# Revit family: EWFLED_AUE03520010001
name_source: partatom
category: Lighting Fixtures
units: mm (PartAtom-declared; Revit-internal decimal feet)

## family parameters
Cut with Voids When Loaded = No
Host = Face
Light Source = Yes
Part Type = Normal
Room Calculation Point = No
Round Connector Dimension = Use Diameter
Shared = No

## types (1)
- EWFLED
    Apparent Load = 240 VA
    Clevertronics Base Angle = 0.00°
    Clevertronics_AS2293 Classification = C0=N/A C90=N/A
    Clevertronics_Annotation Size = 0 mm  [stored 0 ft]
    Clevertronics_Applicable Standards = AS/NZS3820, CISPR15, AS/NZS2293.3
    Clevertronics_Battery = 3.2V 3000mAh
    Clevertronics_Battery Type = Lithium Iron Phosphate
    Clevertronics_Charger Method = Intelligent Current Limited Constant Voltage
    Clevertronics_Construction = Polycarbonate
    Clevertronics_Dimensions Main Enclosure = Main Enclosure - 380mm x 190mm x 130mm // Total Height Including LED Heads 310mm
    Clevertronics_Emergency Driver = 8002976 : Emergency Driver
    Clevertronics_Emergency LED = 1100550 : LED Head
    Clevertronics_Height = 130 mm  [stored 0.426509 ft]
    Clevertronics_IP Rating = IP65
    Clevertronics_Length = 380 mm
    Clevertronics_MIC Number = AUE03520010001
    Clevertronics_Material = Clevertronics_Plycarbonate Base
    Clevertronics_Mounting = Surface Wall Mount (Hard Wired Supply Connection)
    Clevertronics_Operating Mode = Non-maintained
    Clevertronics_Operating Temperature = 0˚C to 40˚C
    Clevertronics_Operating Voltage = 220-240V AC; 50Hz
    Clevertronics_Power Consumption = 0.4W (Standby), 1.3W (Max)
    Clevertronics_Product Description = Supalite IP65 Weatherproof Emergency Floodlight, Trade Series
    Clevertronics_Replacement Battery = 1560156 : Battery
    Clevertronics_Testing System = Manual Test Switch
    Clevertronics_Weight = 2.0kg
    Clevertronics_Width = 190 mm
    Color Filter = 16777215
    Default Elevation = 1200 mm
    Description = Supalite IP65 Weatherproof Emergency Floodlight, Trade Series
    Dimming Lamp Color Temperature Shift = <None>
    Lamp = 2 x LED Heads (Adjustable), 175lm Per Lamp Head
    Manufacturer = Clevertronics
    Model = EWFLED
    Photometric Web File = 6104_EWFLED_IESR_G_202209121543.IES
    Tilt Angle = -90.00°

note: [stored X ft] marks values corroborated as IEEE doubles in the binary element streams (Revit-internal decimal feet)

## geometry (parser evidence)
native form markers: Blend x2, Sweep x8
no freeform markers — native parametric forms only
